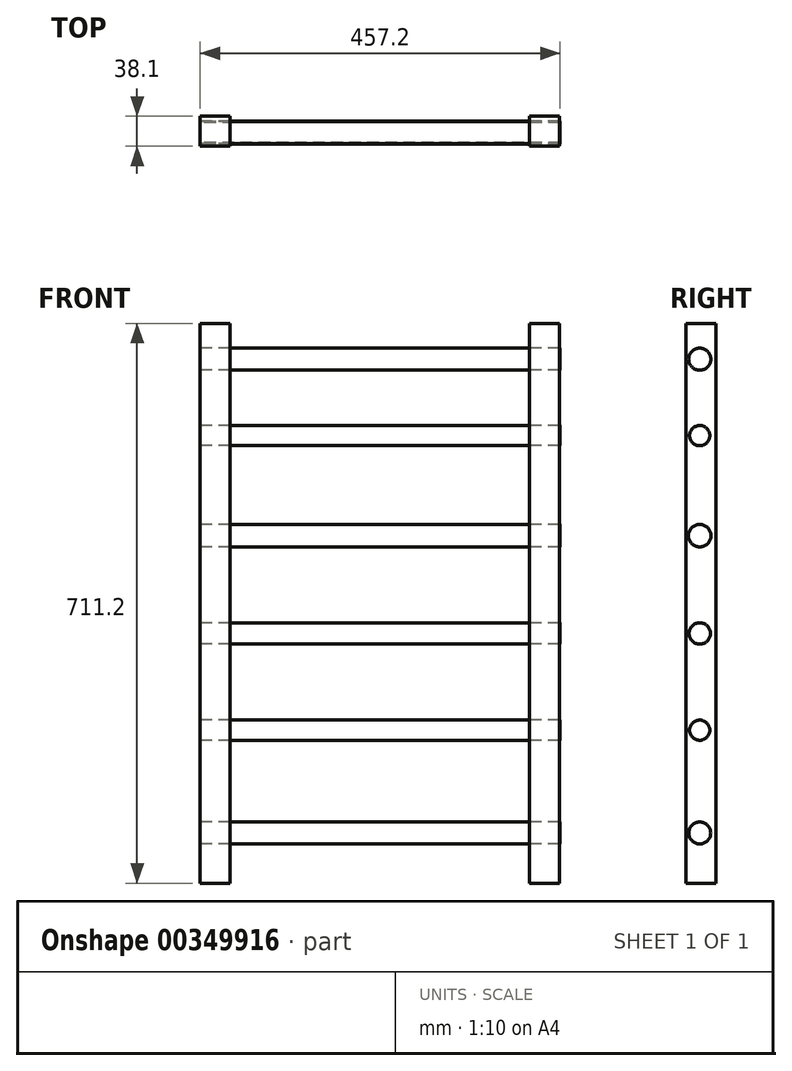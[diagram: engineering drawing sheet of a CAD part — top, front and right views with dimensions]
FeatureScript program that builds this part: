
annotation { "Feature Type Name" : "Feature", "Feature Type Description" : "" }
export const myFeature = defineFeature(function(context is Context, id is Id, definition is map)
    precondition{}
    {
        {
            var Q0;
            Q0=qCreatedBy(makeId("Front.planeOp"),FACE);
            var sketch = newSketch(context, id + "F0", { "sketchPlane" : qUnion([Q0])});
            skLineSegment(sketch, "E0.bottom", {"start": v(-131.8, -63.84) * mm, "end": v(-93.7, -63.84) * mm});
            skLineSegment(sketch, "E0.top", {"start": v(-131.8, 647.36) * mm, "end": v(-93.7, 647.36) * mm});
            skLineSegment(sketch, "E0.left", {"start": v(-131.8, -63.84) * mm, "end": v(-131.8, 647.36) * mm});
            skLineSegment(sketch, "E0.right", {"start": v(-93.7, -63.84) * mm, "end": v(-93.7, 647.36) * mm});
            skLineSegment(sketch, "E1.bottom", {"start": v(324.84, -63.84) * mm, "end": v(286.74, -63.84) * mm});
            skLineSegment(sketch, "E1.top", {"start": v(324.84, 647.36) * mm, "end": v(286.74, 647.36) * mm});
            skLineSegment(sketch, "E1.left", {"start": v(324.84, -63.84) * mm, "end": v(324.84, 647.36) * mm});
            skLineSegment(sketch, "E1.right", {"start": v(286.74, -63.84) * mm, "end": v(286.74, 647.36) * mm});
            skSolve(sketch);
        }
        {
            var Q0;
            Q0 = qSketchRegion(id + "F0", true);
            extrude(context, id + "F1", {"entities" : qUnion([Q0]), "depth" : 38.1 * mm, "offsetDistance" : 25.4 * mm});
        }
        {
            var Q0;
            Q0=makeQuery(id+"F1.opExtrude","SWEPT_FACE",FACE,{"disambiguationData":[OSD([sQuery(id+"F0.wireOp",EDGE,"E0.left")])]});
            var sketch = newSketch(context, id + "F2", { "sketchPlane" : qUnion([Q0])});
            skCircle(sketch, "E2", {"center": v(20.7, 601.9) * mm, "radius": 14.06 * mm});
            skCircle(sketch, "E3", {"center": v(20.7, 504.79) * mm, "radius": 12.85 * mm});
            skCircle(sketch, "E4", {"center": v(20.7, 377.69) * mm, "radius": 14.35 * mm});
            skCircle(sketch, "E5", {"center": v(20.7, 253.45) * mm, "radius": 13.55 * mm});
            skCircle(sketch, "E6", {"center": v(20.7, 130.63) * mm, "radius": 12.85 * mm});
            skCircle(sketch, "E7", {"center": v(20.7, 0) * mm, "radius": 13.9 * mm});
            skSolve(sketch);
        }
        {
            var Q0;
            Q0 = qSketchRegion(id + "F2", true);
            extrude(context, id + "F3", {"entities" : qUnion([Q0]), "oppositeDirection" : true, "depth" : 457.2 * mm, "offsetDistance" : 25.4 * mm});
        }
    });
